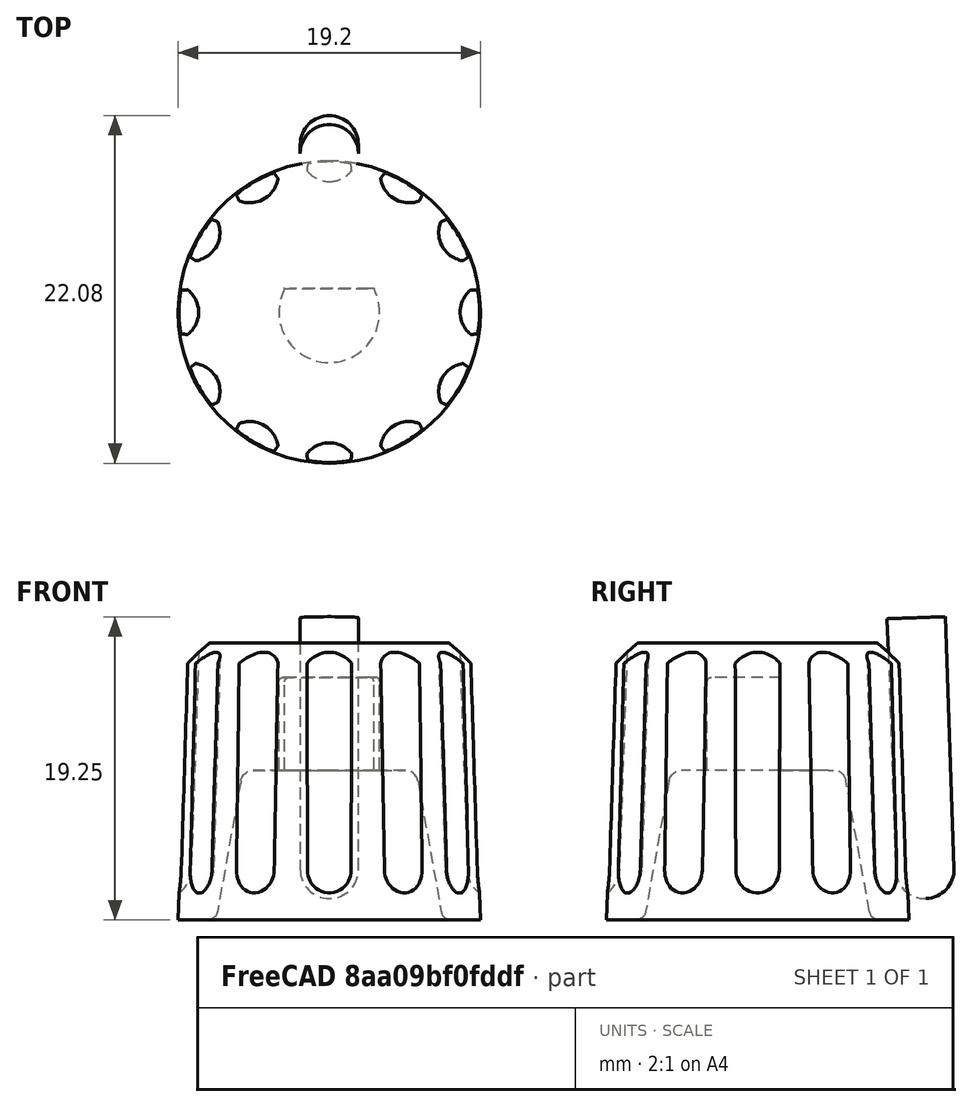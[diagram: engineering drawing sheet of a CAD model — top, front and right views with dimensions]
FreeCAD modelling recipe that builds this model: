
FCSTD DOCUMENT  (FreeCAD 0.21R33771 (Git))
Label: knob_edit24
License: All rights reserved
LicenseURL: http://en.wikipedia.org/wiki/All_rights_reserved
objects: Part::Fuse×2, Sketcher::SketchObject×1, Part::Revolution×1, Part::Cylinder×1, Part::Sphere×1, Part::FeaturePython×1, Part::Cut×1, Part::Box×1
note: 8 computed .brp shape members not serialized (recipe doc carries the construction recipe); baked Part::Feature solids carry a one-line shape summary decoded from their .brp

FEATURE [Sketcher::SketchObject] Sketch
  FullyConstrained = false
  Placement = pos=(0,0,0) rot=(0.57735,0.57735,0.57735;2.0944rad)
  sketch-geometry (15):
    g0: LineSegment StartX=0 StartY=17.6 StartZ=0 EndX=7.5 EndY=17.6 EndZ=0
    g1: LineSegment StartX=9.6 StartY=0 StartZ=0 EndX=9.10139 EndY=16.2546 EndZ=0
    g2: LineSegment StartX=9.06568 StartY=16.3297 StartZ=0 EndX=7.67557 EndY=17.5345 EndZ=0
    g3: LineSegment StartX=7.10721 StartY=0.518508 StartZ=0 EndX=5.61824 EndY=8.83925 EndZ=0
    g4: LineSegment StartX=4.82875 StartY=9.5 StartZ=0 EndX=3.25871 EndY=9.5 EndZ=0
    g5: LineSegment StartX=3.2 StartY=9.55871 StartZ=0 EndX=3.2 EndY=15.1432 EndZ=0
    g6: LineSegment StartX=2.9432 StartY=15.4 StartZ=0 EndX=0 EndY=15.4 EndZ=0
    g7: LineSegment StartX=7.72674 StartY=-7.57945e-10 StartZ=0 EndX=9.6 EndY=-3.45342e-09 EndZ=0
    g8: LineSegment StartX=0 StartY=17.6 StartZ=0 EndX=0 EndY=15.4 EndZ=0
    g9: ArcOfCircle CenterX=7.5 CenterY=17.3319 CenterZ=0 NormalX=0 NormalY=0 NormalZ=1 AngleXU=0 Radius=0.268073 StartAngle=0.856706 EndAngle=1.5708
    g10: ArcOfCircle CenterX=8.99781 CenterY=16.2514 CenterZ=0 NormalX=0 NormalY=0 NormalZ=1 AngleXU=0 Radius=0.10363 StartAngle=0.0306652 EndAngle=0.856706
    g11: ArcOfCircle CenterX=2.9432 CenterY=15.1432 CenterZ=0 NormalX=0 NormalY=0 NormalZ=1 AngleXU=0 Radius=0.256796 StartAngle=0 EndAngle=1.5708
    g12: ArcOfCircle CenterX=7.72674 CenterY=0.629371 CenterZ=0 NormalX=0 NormalY=0 NormalZ=1 AngleXU=0 Radius=0.629371 StartAngle=3.31867 EndAngle=4.71239
    g13: ArcOfCircle CenterX=4.82875 CenterY=8.69797 CenterZ=0 NormalX=0 NormalY=0 NormalZ=1 AngleXU=0 Radius=0.802028 StartAngle=0.177073 EndAngle=1.5708
    g14: ArcOfCircle CenterX=3.25871 CenterY=9.55871 CenterZ=0 NormalX=0 NormalY=0 NormalZ=1 AngleXU=0 Radius=0.058713 StartAngle=3.14159 EndAngle=4.71239
  constraints (14):
    c: PointOnObject(g0,g-2)
    c: Horizontal(g0)
    c: Tangent(g0,g9) = 1.5708
    c: Tangent(g2,g9) = -1.5708
    c: Tangent(g2,g10) = -1.5708
    c: Tangent(g1,g10) = -1.5708
    c: Tangent(g6,g11) = -1.5708
    c: Tangent(g5,g11) = -1.5708
    c: Tangent(g3,g12) = 1.5708
    c: Tangent(g7,g12) = -1.5708
    c: Tangent(g4,g13) = -1.5708
    c: Tangent(g3,g13) = -1.5708
    c: Tangent(g5,g14) = 1.5708
    c: Tangent(g4,g14) = 1.5708
FEATURE [Part::Revolution] Revolve
  Angle = 360
  Axis = (0,0,1)
  Base = (0,0,0)
  FaceMakerClass = Part::FaceMakerBullseye
  Solid = true
  Source = -> Sketch
  Symmetric = false
FEATURE [Part::Cylinder] Cylinder  label="Цилиндр"
  Angle = 360
  AttacherType = Attacher::AttachEngine3D
  FirstAngle = 0
  Height = 16
  Radius = 1.85
  SecondAngle = 0
FEATURE [Part::Sphere] Sphere  label="Сфера"
  Angle1 = -90
  Angle2 = 90
  Angle3 = 360
  AttacherType = Attacher::AttachEngine3D
  Radius = 1.85
FEATURE [Part::Fuse] Fusion
  Base = -> Cylinder
  Placement = pos=(0,10.63,3.2) rot=(1,0,0;0.034907rad)
  Tool = -> Sphere
FEATURE [Part::FeaturePython] Array  # Draft array (typed FeaturePython)
  AlwaysSyncPlacement = false
  Angle = 360
  ArrayType = 1
  Axis = (0,0,1)
  Base = -> Fusion
  Center = (0,0,0)
  Count = 12
  ExpandArray = false
  Fuse = false
  IntervalAxis = (0,0,0)
  IntervalX = (50,0,0)
  IntervalY = (0,50,0)
  IntervalZ = (0,0,50)
  NumberCircles = 3
  NumberPolar = 12
  NumberX = 2
  NumberY = 2
  NumberZ = 1
  PlacementList = 12 placements: [(0,10.63,3.2),(-5.315,9.20585,3.2),(-9.20585,5.315,3.2),(-10.63,0,3.2),(-9.20585,-5.315,3.2),(-5.315,-9.20585,3.2),(-1.3018e-15,-10.63,3.2),(5.315,-9.20585,3.2),(9.20585,-5.315,3.2),(10.63,-1.77636e-15,3.2),(9.20585,5.315,3.2),(5.315,9.20585,3.2)]
  RadialDistance = 50
  ScaleList = (12) [(1,1,1),(1,1,1),(1,1,1),(1,1,1),(1,1,1),(1,1,1),(1,1,1),(1,1,1),(1,1,1),(1,1,1),(1,1,1),(1,1,1)]
  Symmetry = 1
  TangentialDistance = 25
FEATURE [Part::Cut] Cut
  Base = -> Revolve
  Tool = -> Array
FEATURE [Part::Box] Box  label="Куб"
  AttacherType = Attacher::AttachEngine3D
  Height = 6
  Length = 6
  Placement = pos=(-3,1.5,9.5) rot=(0,0,1;0rad)
  Width = 3
FEATURE [Part::Fuse] Fusion001
  Base = -> Cut
  Tool = -> Box
